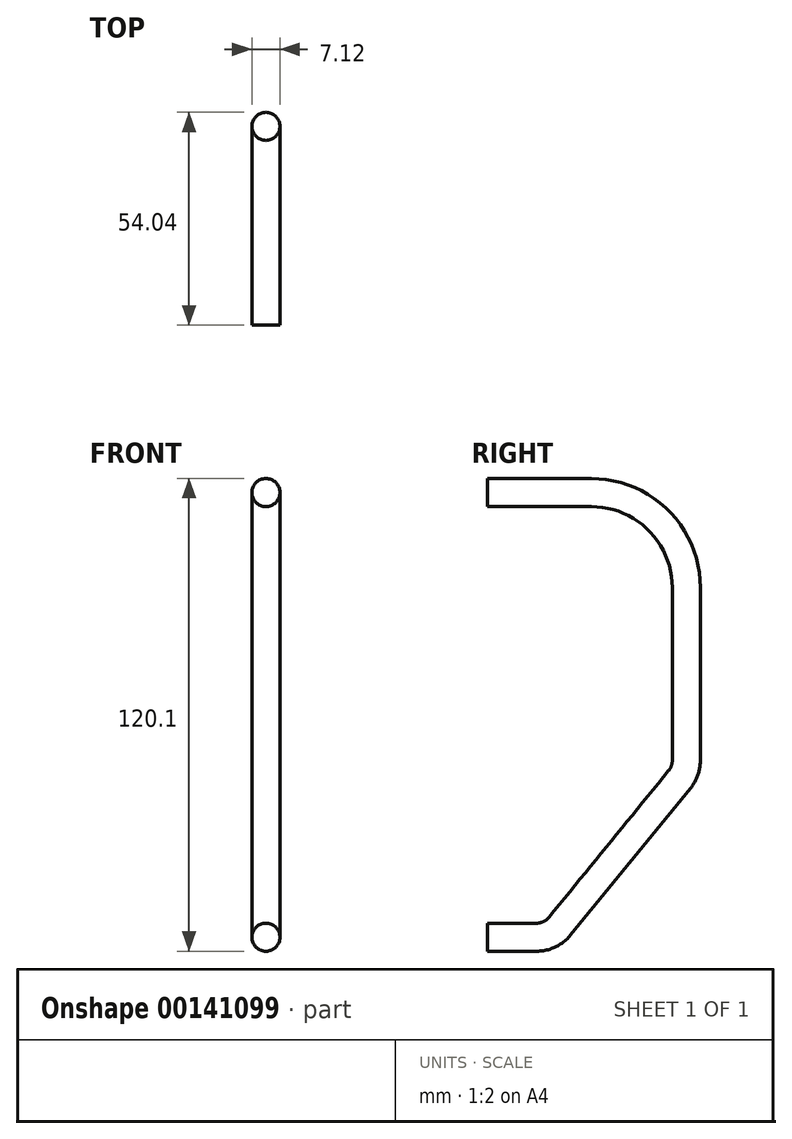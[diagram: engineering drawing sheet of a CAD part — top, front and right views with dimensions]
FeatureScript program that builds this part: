
annotation { "Feature Type Name" : "Feature", "Feature Type Description" : "" }
export const myFeature = defineFeature(function(context is Context, id is Id, definition is map)
    precondition{}
    {
        {
            var Q0;
            Q0=qCreatedBy(makeId("Right.planeOp"),FACE);
            var sketch = newSketch(context, id + "F0", { "sketchPlane" : qUnion([Q0])});
            skLineSegment(sketch, "E0", {"start": v(0, 56.11) * mm, "end": v(26.35, 56.11) * mm});
            skLineSegment(sketch, "E1", {"start": v(50.48, 31.98) * mm, "end": v(50.48, -11.96) * mm});
            skLineSegment(sketch, "E2", {"start": v(48.76, -16.78) * mm, "end": v(18.35, -54.06) * mm});
            skLineSegment(sketch, "E3", {"start": v(12.44, -56.87) * mm, "end": v(0, -56.87) * mm});
            skPoint(sketch, "E4.visualSharp", {"position": v(35.02, 56.11) * mm});
            skPoint(sketch, "E5.visualSharp", {"position": v(50.48, 34.45) * mm});
            skPoint(sketch, "E6.visualSharp", {"position": v(50.48, -14.68) * mm});
            skArc(sketch, "E6.filletArc", {"start": v(48.76, -16.78) * mm, "mid": v(50.04, -14.52) * mm, "end": v(50.48, -11.96) * mm});
            skPoint(sketch, "E7.visualSharp", {"position": v(16.06, -56.87) * mm});
            skArc(sketch, "E7.filletArc", {"start": v(12.44, -56.87) * mm, "mid": v(15.71, -56.13) * mm, "end": v(18.35, -54.06) * mm});
            skArc(sketch, "E8", {"start": v(50.48, 31.98) * mm, "mid": v(43.41, 49.05) * mm, "end": v(26.35, 56.11) * mm});
            skSolve(sketch);
        }
        {
            var Q0;
            Q0=qCreatedBy(makeId("Front.planeOp"),FACE);
            var sketch = newSketch(context, id + "F1", { "sketchPlane" : qUnion([Q0])});
            skCircle(sketch, "E9", {"center": v(0, 1033.4) * mm, "radius": 19.05 * mm});
            skCircle(sketch, "E10", {"center": v(0, 56.11) * mm, "radius": 3.56 * mm});
            skSolve(sketch);
        }
        {
            var Q0;
            Q0=makeQuery(id+"F1.imprint","IMPRINT",FACE,{"disambiguationData":[TD([[makeQuery(id+"F1.imprint","IMPRINT",EDGE,{"derivedFrom":sQuery(id+"F1.wireOp",EDGE,"E10")}),1.0]])]});
            var Q1;
            Q1=sQuery(id+"F0.wireOp",EDGE,"E0");
            var Q2;
            Q2=sQuery(id+"F0.wireOp",EDGE,"E8");
            var Q3;
            Q3=sQuery(id+"F0.wireOp",EDGE,"E1");
            var Q4;
            Q4=sQuery(id+"F0.wireOp",EDGE,"E6.filletArc");
            var Q5;
            Q5=sQuery(id+"F0.wireOp",EDGE,"E2");
            var Q6;
            Q6=sQuery(id+"F0.wireOp",EDGE,"E7.filletArc");
            var Q7;
            Q7=sQuery(id+"F0.wireOp",EDGE,"E3");
            sweep(context, id + "F2", {"profiles" : qUnion([Q0]), "path" : qUnion([Q1, Q2, Q3, Q4, Q5, Q6, Q7])});
        }
    });
